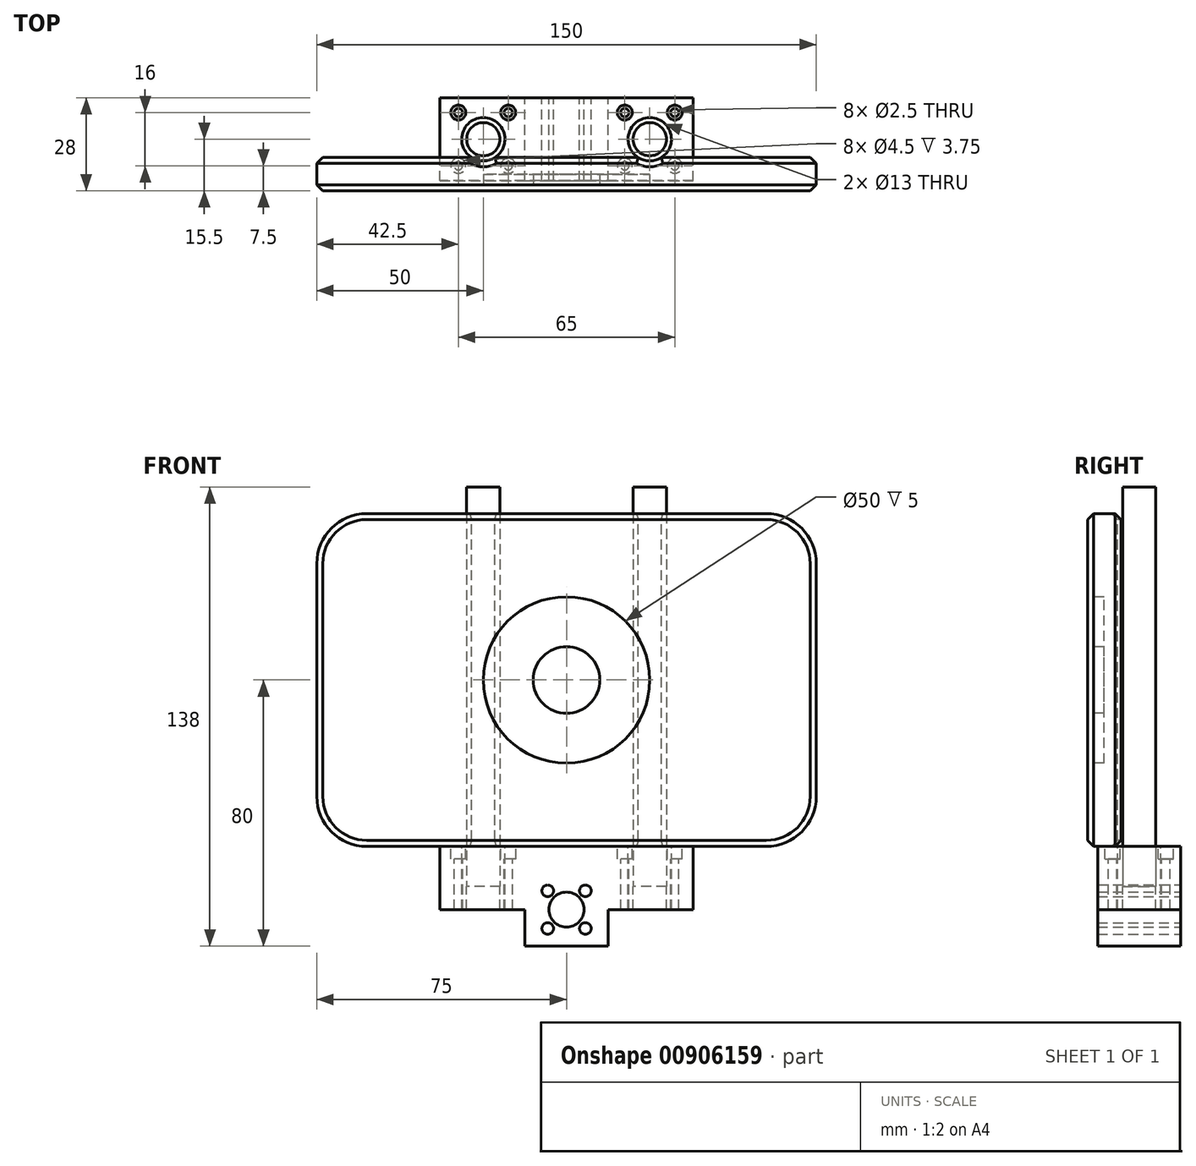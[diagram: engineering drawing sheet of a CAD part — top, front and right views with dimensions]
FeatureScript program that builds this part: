
annotation { "Feature Type Name" : "Feature", "Feature Type Description" : "" }
export const myFeature = defineFeature(function(context is Context, id is Id, definition is map)
    precondition{}
    {
        {
            var Q0;
            Q0=qCreatedBy(makeId("Front.planeOp"),FACE);
            var sketch = newSketch(context, id + "F0", { "sketchPlane" : qUnion([Q0])});
            skLineSegment(sketch, "E0", {"start": v(38, 30) * mm, "end": v(-38, 30) * mm});
            skLineSegment(sketch, "E1", {"start": v(-38, 30) * mm, "end": v(-38, 11) * mm});
            skLineSegment(sketch, "E2", {"start": v(-38, 11) * mm, "end": v(-12.5, 11) * mm});
            skLineSegment(sketch, "E3", {"start": v(-12.5, 11) * mm, "end": v(-12.5, 0) * mm});
            skLineSegment(sketch, "E4", {"start": v(-12.5, 0) * mm, "end": v(12.5, 0) * mm});
            skLineSegment(sketch, "E5", {"start": v(12.5, 0) * mm, "end": v(12.5, 11) * mm});
            skLineSegment(sketch, "E6", {"start": v(12.5, 11) * mm, "end": v(38, 11) * mm});
            skLineSegment(sketch, "E7", {"start": v(38, 11) * mm, "end": v(38, 30) * mm});
            skCircle(sketch, "E8", {"center": v(0, 11) * mm, "radius": 5.25 * mm});
            skCircle(sketch, "E9", {"center": v(0, 11) * mm, "radius": 8 * mm, "construction": true});
            skCircle(sketch, "E10", {"center": v(5.66, 5.34) * mm, "radius": 1.75 * mm});
            skCircle(sketch, "E11", {"center": v(-5.66, 5.34) * mm, "radius": 1.75 * mm});
            skCircle(sketch, "E12", {"center": v(-5.66, 16.66) * mm, "radius": 1.75 * mm});
            skLineSegment(sketch, "E13", {"start": v(-5.66, 16.66) * mm, "end": v(5.66, 5.34) * mm, "construction": true});
            skLineSegment(sketch, "E14", {"start": v(5.66, 16.66) * mm, "end": v(-5.66, 5.34) * mm, "construction": true});
            skLineSegment(sketch, "E15", {"start": v(0, 11) * mm, "end": v(0, 19) * mm, "construction": true});
            skCircle(sketch, "E16", {"center": v(5.66, 16.66) * mm, "radius": 1.75 * mm});
            skSolve(sketch);
        }
        {
            var Q0;
            Q0 = qSketchRegion(id + "F0", true);
            extrude(context, id + "F1", {"entities" : qUnion([Q0]), "depth" : 25 * mm, "offsetDistance" : 25 * mm});
        }
        {
            var Q0;
            Q0=makeQuery(id+"F1.opExtrude","SWEPT_FACE",FACE,{"disambiguationData":[OSD([sQuery(id+"F0.wireOp",EDGE,"E0")])]});
            var sketch = newSketch(context, id + "F2", { "sketchPlane" : qUnion([Q0])});
            skLineSegment(sketch, "E17.bottom", {"start": v(-32.5, -20.5) * mm, "end": v(-17.5, -20.5) * mm, "construction": true});
            skLineSegment(sketch, "E17.top", {"start": v(-32.5, -4.5) * mm, "end": v(-17.5, -4.5) * mm, "construction": true});
            skLineSegment(sketch, "E17.left", {"start": v(-32.5, -20.5) * mm, "end": v(-32.5, -4.5) * mm, "construction": true});
            skLineSegment(sketch, "E17.right", {"start": v(-17.5, -20.5) * mm, "end": v(-17.5, -4.5) * mm, "construction": true});
            skLineSegment(sketch, "E18.bottom", {"start": v(32.5, -20.5) * mm, "end": v(17.5, -20.5) * mm, "construction": true});
            skLineSegment(sketch, "E18.top", {"start": v(32.5, -4.5) * mm, "end": v(17.5, -4.5) * mm, "construction": true});
            skLineSegment(sketch, "E18.left", {"start": v(32.5, -20.5) * mm, "end": v(32.5, -4.5) * mm, "construction": true});
            skLineSegment(sketch, "E18.right", {"start": v(17.5, -20.5) * mm, "end": v(17.5, -4.5) * mm, "construction": true});
            skCircle(sketch, "E19", {"center": v(-17.5, -4.5) * mm, "radius": 1.25 * mm});
            skCircle(sketch, "E20", {"center": v(-17.5, -20.5) * mm, "radius": 1.25 * mm});
            skCircle(sketch, "E21", {"center": v(-32.5, -20.5) * mm, "radius": 1.25 * mm});
            skCircle(sketch, "E22", {"center": v(-32.5, -4.5) * mm, "radius": 1.25 * mm});
            skCircle(sketch, "E23", {"center": v(17.5, -20.5) * mm, "radius": 1.25 * mm});
            skCircle(sketch, "E24", {"center": v(17.5, -4.5) * mm, "radius": 1.25 * mm});
            skCircle(sketch, "E25", {"center": v(32.5, -4.5) * mm, "radius": 1.25 * mm});
            skCircle(sketch, "E26", {"center": v(32.5, -20.5) * mm, "radius": 1.25 * mm});
            skLineSegment(sketch, "E27", {"start": v(-38, -12.5) * mm, "end": v(38, -12.5) * mm, "construction": true});
            skLineSegment(sketch, "E28", {"start": v(0, 0) * mm, "end": v(0, -25) * mm, "construction": true});
            skLineSegment(sketch, "E29", {"start": v(-25, -4.5) * mm, "end": v(-25, -20.5) * mm, "construction": true});
            skLineSegment(sketch, "E30", {"start": v(25, -4.5) * mm, "end": v(25, -20.5) * mm, "construction": true});
            skCircle(sketch, "E31", {"center": v(-32.5, -4.5) * mm, "radius": 2.25 * mm});
            skCircle(sketch, "E32", {"center": v(-17.5, -4.5) * mm, "radius": 2.25 * mm});
            skCircle(sketch, "E33", {"center": v(-17.5, -20.5) * mm, "radius": 2.25 * mm});
            skCircle(sketch, "E34", {"center": v(-32.5, -20.5) * mm, "radius": 2.25 * mm});
            skCircle(sketch, "E35", {"center": v(17.5, -4.5) * mm, "radius": 2.25 * mm});
            skCircle(sketch, "E36", {"center": v(32.5, -4.5) * mm, "radius": 2.25 * mm});
            skCircle(sketch, "E37", {"center": v(32.5, -20.5) * mm, "radius": 2.25 * mm});
            skCircle(sketch, "E38", {"center": v(17.5, -20.5) * mm, "radius": 2.25 * mm});
            skSolve(sketch);
        }
        {
            var Q0;
            Q0=makeQuery(id+"F2.imprint","IMPRINT",FACE,{"disambiguationData":[TD([[makeQuery(id+"F2.imprint","IMPRINT",EDGE,{"derivedFrom":sQuery(id+"F2.wireOp",EDGE,"E21")}),1.0]])]});
            var Q1;
            Q1=makeQuery(id+"F2.imprint","IMPRINT",FACE,{"disambiguationData":[TD([[makeQuery(id+"F2.imprint","IMPRINT",EDGE,{"derivedFrom":sQuery(id+"F2.wireOp",EDGE,"E22")}),1.0]])]});
            var Q2;
            Q2=makeQuery(id+"F2.imprint","IMPRINT",FACE,{"disambiguationData":[TD([[makeQuery(id+"F2.imprint","IMPRINT",EDGE,{"derivedFrom":sQuery(id+"F2.wireOp",EDGE,"E19")}),1.0]])]});
            var Q3;
            Q3=makeQuery(id+"F2.imprint","IMPRINT",FACE,{"disambiguationData":[TD([[makeQuery(id+"F2.imprint","IMPRINT",EDGE,{"derivedFrom":sQuery(id+"F2.wireOp",EDGE,"E20")}),1.0]])]});
            var Q4;
            Q4=makeQuery(id+"F2.imprint","IMPRINT",FACE,{"disambiguationData":[TD([[makeQuery(id+"F2.imprint","IMPRINT",EDGE,{"derivedFrom":sQuery(id+"F2.wireOp",EDGE,"E24")}),1.0]])]});
            var Q5;
            Q5=makeQuery(id+"F2.imprint","IMPRINT",FACE,{"disambiguationData":[TD([[makeQuery(id+"F2.imprint","IMPRINT",EDGE,{"derivedFrom":sQuery(id+"F2.wireOp",EDGE,"E23")}),1.0]])]});
            var Q6;
            Q6=makeQuery(id+"F2.imprint","IMPRINT",FACE,{"disambiguationData":[TD([[makeQuery(id+"F2.imprint","IMPRINT",EDGE,{"derivedFrom":sQuery(id+"F2.wireOp",EDGE,"E26")}),1.0]])]});
            var Q7;
            Q7=makeQuery(id+"F2.imprint","IMPRINT",FACE,{"disambiguationData":[TD([[makeQuery(id+"F2.imprint","IMPRINT",EDGE,{"derivedFrom":sQuery(id+"F2.wireOp",EDGE,"E25")}),1.0]])]});
            extrude(context, id + "F3", {"entities" : qUnion([Q0, Q1, Q2, Q3, Q4, Q5, Q6, Q7]), "operationType" : NewBodyOperationType.REMOVE, "endBound" : BoundingType.UP_TO_NEXT, "oppositeDirection" : true, "depth" : 25 * mm, "offsetDistance" : 25 * mm});
        }
        {
            var Q0;
            Q0=makeQuery(id+"F2.imprint","IMPRINT",FACE,{"disambiguationData":[TD([[makeQuery(id+"F2.imprint","IMPRINT",EDGE,{"derivedFrom":sQuery(id+"F2.wireOp",EDGE,"E24")}),-1.0]])]});
            var Q1;
            Q1=makeQuery(id+"F2.imprint","IMPRINT",FACE,{"disambiguationData":[TD([[makeQuery(id+"F2.imprint","IMPRINT",EDGE,{"derivedFrom":sQuery(id+"F2.wireOp",EDGE,"E23")}),-1.0]])]});
            var Q2;
            Q2=makeQuery(id+"F2.imprint","IMPRINT",FACE,{"disambiguationData":[TD([[makeQuery(id+"F2.imprint","IMPRINT",EDGE,{"derivedFrom":sQuery(id+"F2.wireOp",EDGE,"E26")}),-1.0]])]});
            var Q3;
            Q3=makeQuery(id+"F2.imprint","IMPRINT",FACE,{"disambiguationData":[TD([[makeQuery(id+"F2.imprint","IMPRINT",EDGE,{"derivedFrom":sQuery(id+"F2.wireOp",EDGE,"E25")}),-1.0]])]});
            var Q4;
            Q4=makeQuery(id+"F2.imprint","IMPRINT",FACE,{"disambiguationData":[TD([[makeQuery(id+"F2.imprint","IMPRINT",EDGE,{"derivedFrom":sQuery(id+"F2.wireOp",EDGE,"E22")}),-1.0]])]});
            var Q5;
            Q5=makeQuery(id+"F2.imprint","IMPRINT",FACE,{"disambiguationData":[TD([[makeQuery(id+"F2.imprint","IMPRINT",EDGE,{"derivedFrom":sQuery(id+"F2.wireOp",EDGE,"E19")}),-1.0]])]});
            var Q6;
            Q6=makeQuery(id+"F2.imprint","IMPRINT",FACE,{"disambiguationData":[TD([[makeQuery(id+"F2.imprint","IMPRINT",EDGE,{"derivedFrom":sQuery(id+"F2.wireOp",EDGE,"E20")}),-1.0]])]});
            var Q7;
            Q7=makeQuery(id+"F2.imprint","IMPRINT",FACE,{"disambiguationData":[TD([[makeQuery(id+"F2.imprint","IMPRINT",EDGE,{"derivedFrom":sQuery(id+"F2.wireOp",EDGE,"E21")}),-1.0]])]});
            extrude(context, id + "F4", {"entities" : qUnion([Q0, Q1, Q2, Q3, Q4, Q5, Q6, Q7]), "operationType" : NewBodyOperationType.REMOVE, "oppositeDirection" : true, "depth" : 3.75 * mm, "offsetDistance" : 25 * mm});
        }
        {
            var Q0;
            Q0=makeQuery(id+"F1.opExtrude","SWEPT_FACE",FACE,{"disambiguationData":[OSD([sQuery(id+"F0.wireOp",EDGE,"E0")])]});
            var sketch = newSketch(context, id + "F5", { "sketchPlane" : qUnion([Q0])});
            skCircle(sketch, "E39", {"center": v(-25, -12.5) * mm, "radius": 5.2 * mm});
            skCircle(sketch, "E40", {"center": v(25, -12.5) * mm, "radius": 5.2 * mm});
            skLineSegment(sketch, "E41", {"start": v(-32.5, -4.5) * mm, "end": v(-17.5, -20.5) * mm, "construction": true});
            skLineSegment(sketch, "E42", {"start": v(-17.5, -4.5) * mm, "end": v(-32.5, -20.5) * mm, "construction": true});
            skLineSegment(sketch, "E43", {"start": v(32.5, -4.5) * mm, "end": v(17.5, -20.5) * mm, "construction": true});
            skLineSegment(sketch, "E44", {"start": v(17.5, -4.5) * mm, "end": v(32.5, -20.5) * mm, "construction": true});
            skSolve(sketch);
        }
        {
            var Q0;
            Q0 = qSketchRegion(id + "F5", true);
            extrude(context, id + "F6", {"entities" : qUnion([Q0]), "operationType" : NewBodyOperationType.REMOVE, "oppositeDirection" : true, "depth" : 12 * mm, "offsetDistance" : 25 * mm});
        }
        {
            var Q0;
            Q0=makeQuery(id+"F6.boolean.opBoolean","COPY",FACE,{"derivedFrom":makeQuery(id+"F6.opExtrude","CAP_FACE",FACE,{"disambiguationData":[OSD([sQuery(id+"F5.wireOp",EDGE,"E39")])],"isStart":false})});
            var sketch = newSketch(context, id + "F7", { "sketchPlane" : qUnion([Q0])});
            skCircle(sketch, "E45", {"center": v(-25, -12.5) * mm, "radius": 5 * mm});
            skCircle(sketch, "E46", {"center": v(25, -12.5) * mm, "radius": 5 * mm});
            skSolve(sketch);
        }
        {
            var Q0;
            Q0 = qSketchRegion(id + "F7", true);
            extrude(context, id + "F8", {"entities" : qUnion([Q0]), "depth" : 120 * mm, "offsetDistance" : 25 * mm});
        }
        {
            var Q0;
            Q0=makeQuery(id+"F1.opExtrude","SWEPT_FACE",FACE,{"disambiguationData":[OSD([sQuery(id+"F0.wireOp",EDGE,"E0")])]});
            cPlane(context, id + "F9", {"entities" : qUnion([Q0]), "cplaneType" : CPlaneType.OFFSET, "offset" : 25 * mm, "width" : 150 * mm, "height" : 150 * mm});
        }
        {
            var Q0;
            Q0=qCreatedBy(id+"F9.planeOp",FACE);
            var sketch = newSketch(context, id + "F10", { "sketchPlane" : qUnion([Q0])});
            skCircle(sketch, "E47", {"center": v(25, -12.5) * mm, "radius": 5 * mm});
            skCircle(sketch, "E48", {"center": v(-25, -12.5) * mm, "radius": 5 * mm});
            skCircle(sketch, "E49", {"center": v(25, -12.5) * mm, "radius": 6.5 * mm});
            skCircle(sketch, "E50", {"center": v(-25, -12.5) * mm, "radius": 6.5 * mm});
            skSolve(sketch);
        }
        {
            var Q0;
            Q0 = qSketchRegion(id + "F10", true);
            extrude(context, id + "F11", {"entities" : qUnion([Q0]), "depth" : 25 * mm, "offsetDistance" : 25 * mm});
        }
        {
            var Q0;
            Q0=makeQuery(id+"F1.opExtrude","CAP_FACE",FACE,{"disambiguationData":[OSD([sQuery(id+"F0.wireOp",EDGE,"E0"),sQuery(id+"F0.wireOp",EDGE,"E1"),sQuery(id+"F0.wireOp",EDGE,"E2"),sQuery(id+"F0.wireOp",EDGE,"E3"),sQuery(id+"F0.wireOp",EDGE,"E4"),sQuery(id+"F0.wireOp",EDGE,"E5"),sQuery(id+"F0.wireOp",EDGE,"E6"),sQuery(id+"F0.wireOp",EDGE,"E7"),sQuery(id+"F0.wireOp",EDGE,"E8"),sQuery(id+"F0.wireOp",EDGE,"E10"),sQuery(id+"F0.wireOp",EDGE,"E11"),sQuery(id+"F0.wireOp",EDGE,"E12"),sQuery(id+"F0.wireOp",EDGE,"E16")])],"isStart":false});
            cPlane(context, id + "F12", {"entities" : qUnion([Q0]), "cplaneType" : CPlaneType.OFFSET, "offset" : 7 * mm, "oppositeDirection" : true, "width" : 150 * mm, "height" : 150 * mm});
        }
        {
            var Q0;
            Q0=qCreatedBy(id+"F12.planeOp",FACE);
            var sketch = newSketch(context, id + "F13", { "sketchPlane" : qUnion([Q0])});
            skLineSegment(sketch, "E51.bottom", {"start": v(-75, 30) * mm, "end": v(75, 30) * mm});
            skLineSegment(sketch, "E51.top", {"start": v(-75, 130) * mm, "end": v(75, 130) * mm});
            skLineSegment(sketch, "E51.left", {"start": v(-75, 30) * mm, "end": v(-75, 130) * mm});
            skLineSegment(sketch, "E51.right", {"start": v(75, 30) * mm, "end": v(75, 130) * mm});
            skSolve(sketch);
        }
        {
            var Q0;
            Q0 = qSketchRegion(id + "F13", true);
            extrude(context, id + "F14", {"entities" : qUnion([Q0]), "depth" : 10 * mm, "offsetDistance" : 25 * mm});
        }
        {
            var Q0;
            Q0=makeQuery(id+"F14.opExtrude","CAP_FACE",FACE,{"disambiguationData":[OSD([sQuery(id+"F13.wireOp",EDGE,"E51.bottom"),sQuery(id+"F13.wireOp",EDGE,"E51.top"),sQuery(id+"F13.wireOp",EDGE,"E51.left"),sQuery(id+"F13.wireOp",EDGE,"E51.right")])],"isStart":false});
            var sketch = newSketch(context, id + "F15", { "sketchPlane" : qUnion([Q0])});
            skCircle(sketch, "E52", {"center": v(0, 80) * mm, "radius": 25 * mm});
            skLineSegment(sketch, "E53", {"start": v(-75, 30) * mm, "end": v(75, 130) * mm, "construction": true});
            skLineSegment(sketch, "E54", {"start": v(75, 30) * mm, "end": v(-75, 130) * mm, "construction": true});
            skCircle(sketch, "E55", {"center": v(0, 80) * mm, "radius": 10 * mm});
            skSolve(sketch);
        }
        {
            var Q0;
            Q0 = qSketchRegion(id + "F15", true);
            extrude(context, id + "F16", {"entities" : qUnion([Q0]), "operationType" : NewBodyOperationType.REMOVE, "oppositeDirection" : true, "depth" : 5 * mm, "offsetDistance" : 25 * mm});
        }
        {
            var Q0;
            Q0 = qSketchRegion(id + "F10", true);
            extrude(context, id + "F17", {"entities" : qUnion([Q0]), "operationType" : NewBodyOperationType.REMOVE, "endBound" : BoundingType.THROUGH_ALL, "oppositeDirection" : true, "depth" : 25 * mm, "offsetDistance" : 25 * mm, "hasSecondDirection" : true, "secondDirectionBound" : SecondDirectionBoundingType.THROUGH_ALL, "secondDirectionOppositeDirection" : false, "secondDirectionDepth" : 25 * mm});
        }
        {
            var Q0;
            Q0=makeQuery(id+"F14.opExtrude","SWEPT_EDGE",EDGE,{"disambiguationData":[OSD([sQuery(id+"F13.wireOp",EDGE,"E51.top"),sQuery(id+"F13.wireOp",EDGE,"E51.left")])]});
            var Q1;
            Q1=makeQuery(id+"F14.opExtrude","SWEPT_EDGE",EDGE,{"disambiguationData":[OSD([sQuery(id+"F13.wireOp",EDGE,"E51.bottom"),sQuery(id+"F13.wireOp",EDGE,"E51.left")])]});
            var Q2;
            Q2=makeQuery(id+"F14.opExtrude","SWEPT_EDGE",EDGE,{"disambiguationData":[OSD([sQuery(id+"F13.wireOp",EDGE,"E51.bottom"),sQuery(id+"F13.wireOp",EDGE,"E51.right")])]});
            var Q3;
            Q3=makeQuery(id+"F14.opExtrude","SWEPT_EDGE",EDGE,{"disambiguationData":[OSD([sQuery(id+"F13.wireOp",EDGE,"E51.top"),sQuery(id+"F13.wireOp",EDGE,"E51.right")])]});
            fillet(context, id + "F18", {"entities" : qUnion([Q0, Q1, Q2, Q3]), "radius" : 15 * mm, "tangentPropagation" : true, "allowEdgeOverflow" : false});
        }
        {
            var Q0;
            Q0=makeQuery(id+"F14.opExtrude","SWEPT_FACE",FACE,{"disambiguationData":[OSD([sQuery(id+"F13.wireOp",EDGE,"E51.top")])]});
            var Q1;
            Q1=makeQuery(id+"F18.opFillet","BLEND_FACE",FACE,{"disambiguationData":[OSD([sQuery(id+"F13.wireOp",EDGE,"E51.top"),sQuery(id+"F13.wireOp",EDGE,"E51.left")])]});
            var Q2;
            Q2=makeQuery(id+"F14.opExtrude","SWEPT_FACE",FACE,{"disambiguationData":[OSD([sQuery(id+"F13.wireOp",EDGE,"E51.left")])]});
            var Q3;
            Q3=makeQuery(id+"F18.opFillet","BLEND_FACE",FACE,{"disambiguationData":[OSD([sQuery(id+"F13.wireOp",EDGE,"E51.bottom"),sQuery(id+"F13.wireOp",EDGE,"E51.left")])]});
            var Q4;
            Q4=makeQuery(id+"F14.opExtrude","SWEPT_FACE",FACE,{"disambiguationData":[OSD([sQuery(id+"F13.wireOp",EDGE,"E51.bottom")])]});
            var Q5;
            Q5=makeQuery(id+"F18.opFillet","BLEND_FACE",FACE,{"disambiguationData":[OSD([sQuery(id+"F13.wireOp",EDGE,"E51.bottom"),sQuery(id+"F13.wireOp",EDGE,"E51.right")])]});
            var Q6;
            Q6=makeQuery(id+"F14.opExtrude","SWEPT_FACE",FACE,{"disambiguationData":[OSD([sQuery(id+"F13.wireOp",EDGE,"E51.right")])]});
            var Q7;
            Q7=makeQuery(id+"F18.opFillet","BLEND_FACE",FACE,{"disambiguationData":[OSD([sQuery(id+"F13.wireOp",EDGE,"E51.top"),sQuery(id+"F13.wireOp",EDGE,"E51.right")])]});
            chamfer(context, id + "F19", {"entities" : qUnion([Q0, Q1, Q2, Q3, Q4, Q5, Q6, Q7]), "width" : 1.8 * mm, "tangentPropagation" : true});
        }
    });
